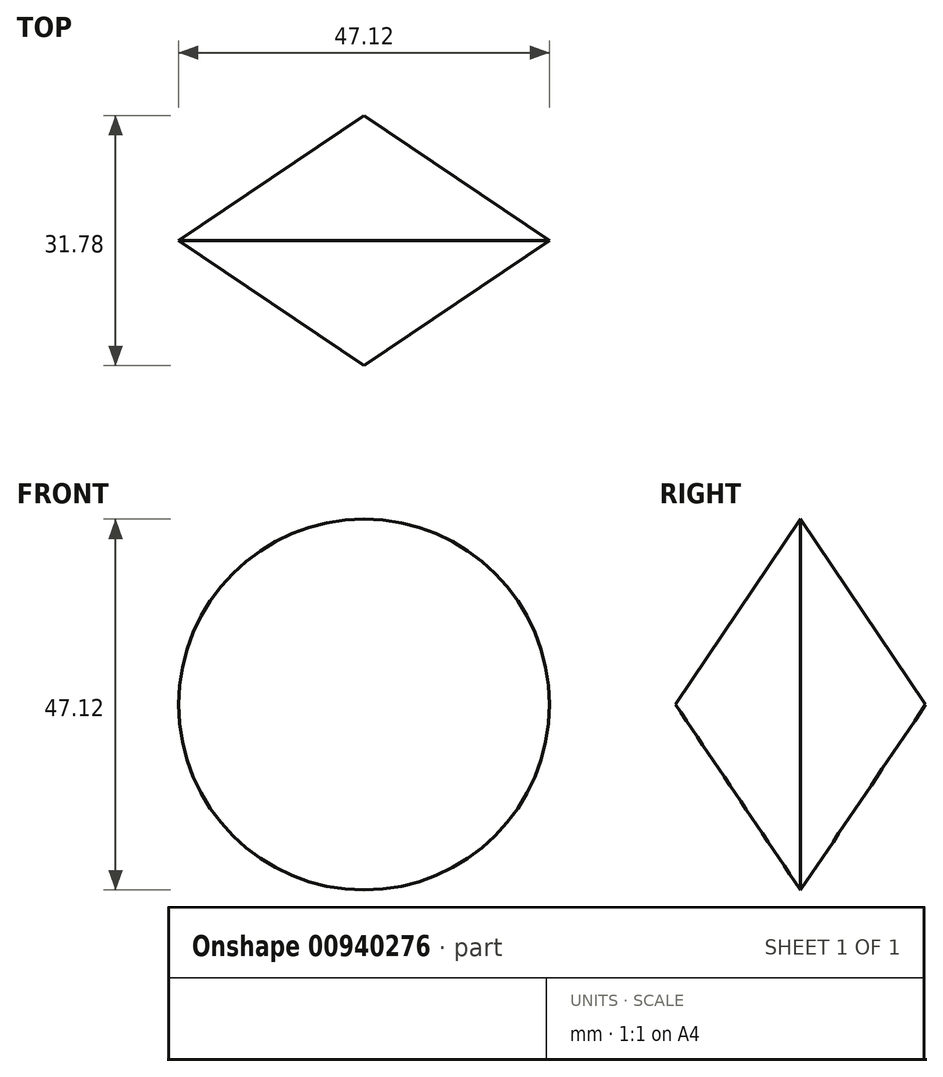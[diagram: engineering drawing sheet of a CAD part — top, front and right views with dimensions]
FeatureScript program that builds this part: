
annotation { "Feature Type Name" : "Feature", "Feature Type Description" : "" }
export const myFeature = defineFeature(function(context is Context, id is Id, definition is map)
    precondition{}
    {
        {
            var Q0;
            Q0=qCreatedBy(makeId("Front.planeOp"),FACE);
            var sketch = newSketch(context, id + "F0", { "sketchPlane" : qUnion([Q0])});
            skCircle(sketch, "E0", {"center": v(0, 0) * mm, "radius": 23.56 * mm});
            skSolve(sketch);
        }
        {
            var Q0;
            Q0 = qSketchRegion(id + "F0", true);
            extrude(context, id + "F1", {"entities" : qUnion([Q0]), "depth" : 25.4 * mm, "offsetDistance" : 25.4 * mm, "hasDraft" : true, "draftAngle" : 56 * degree, "draftPullDirection" : true});
        }
        {
            var Q0;
            Q0=makeQuery(id+"F1.opExtrude","SWEPT_BODY",BODY,{"disambiguationData":[OSD([sQuery(id+"F0.wireOp",EDGE,"E0")])]});
            var Q1;
            Q1=qCreatedBy(makeId("Front.planeOp"),FACE);
            mirror(context, id + "F2", {"operationType" : NewBodyOperationType.ADD, "entities" : qUnion([Q0]), "mirrorPlane" : qUnion([Q1])});
        }
    });
